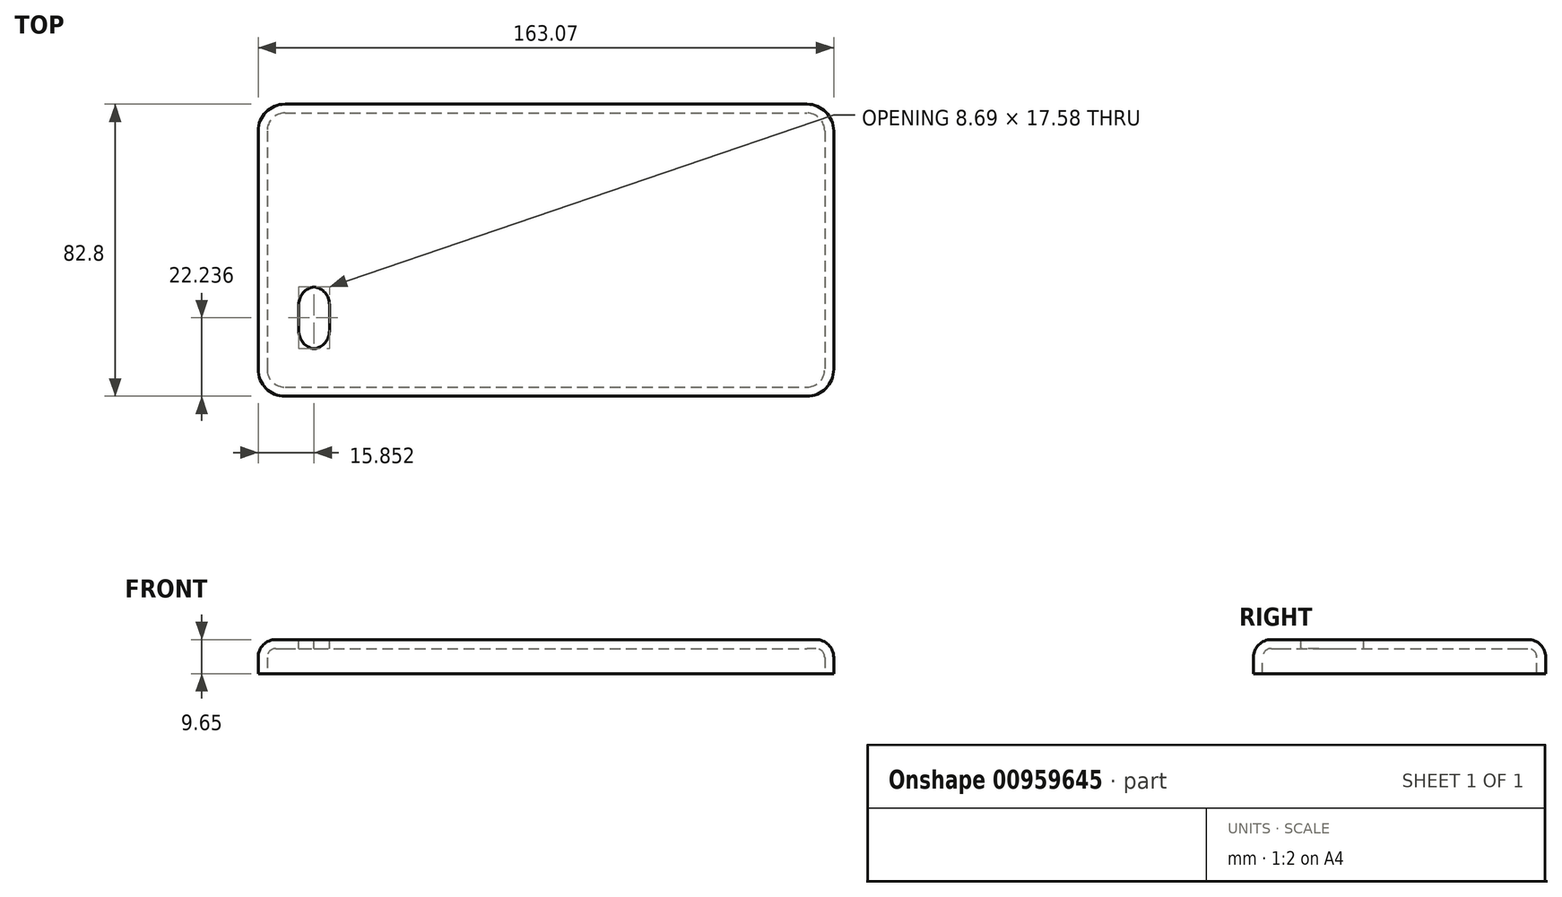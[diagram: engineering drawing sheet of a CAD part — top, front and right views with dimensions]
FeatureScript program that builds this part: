
annotation { "Feature Type Name" : "Feature", "Feature Type Description" : "" }
export const myFeature = defineFeature(function(context is Context, id is Id, definition is map)
    precondition{}
    {
        {
            var Q0;
            Q0=qCreatedBy(makeId("Top.planeOp"),FACE);
            var sketch = newSketch(context, id + "F0", { "sketchPlane" : qUnion([Q0])});
            skLineSegment(sketch, "E0.bottom", {"start": v(0, 0) * mm, "end": v(163.07, 0) * mm});
            skLineSegment(sketch, "E0.top", {"start": v(0, -82.8) * mm, "end": v(163.07, -82.8) * mm});
            skLineSegment(sketch, "E0.left", {"start": v(0, 0) * mm, "end": v(0, -82.8) * mm});
            skLineSegment(sketch, "E0.right", {"start": v(163.07, 0) * mm, "end": v(163.07, -82.8) * mm});
            skSolve(sketch);
        }
        {
            var Q0;
            Q0 = qSketchRegion(id + "F0", true);
            extrude(context, id + "F1", {"entities" : qUnion([Q0]), "depth" : 9.65 * mm, "offsetDistance" : 25.4 * mm});
        }
        {
            var Q0;
            Q0=makeQuery(id+"F1.opExtrude","SWEPT_EDGE",EDGE,{"disambiguationData":[OSD([sQuery(id+"F0.wireOp",EDGE,"E0.bottom"),sQuery(id+"F0.wireOp",EDGE,"E0.left")])]});
            var Q1;
            Q1=makeQuery(id+"F1.opExtrude","SWEPT_EDGE",EDGE,{"disambiguationData":[OSD([sQuery(id+"F0.wireOp",EDGE,"E0.bottom"),sQuery(id+"F0.wireOp",EDGE,"E0.right")])]});
            var Q2;
            Q2=makeQuery(id+"F1.opExtrude","SWEPT_EDGE",EDGE,{"disambiguationData":[OSD([sQuery(id+"F0.wireOp",EDGE,"E0.top"),sQuery(id+"F0.wireOp",EDGE,"E0.right")])]});
            var Q3;
            Q3=makeQuery(id+"F1.opExtrude","SWEPT_EDGE",EDGE,{"disambiguationData":[OSD([sQuery(id+"F0.wireOp",EDGE,"E0.top"),sQuery(id+"F0.wireOp",EDGE,"E0.left")])]});
            fillet(context, id + "F2", {"entities" : qUnion([Q0, Q1, Q2, Q3]), "radius" : 7.62 * mm, "tangentPropagation" : true, "allowEdgeOverflow" : false});
        }
        {
            var Q0;
            Q0=makeQuery(id+"F1.opExtrude","CAP_FACE",FACE,{"disambiguationData":[OSD([sQuery(id+"F0.wireOp",EDGE,"E0.bottom"),sQuery(id+"F0.wireOp",EDGE,"E0.top"),sQuery(id+"F0.wireOp",EDGE,"E0.left"),sQuery(id+"F0.wireOp",EDGE,"E0.right")])],"isStart":false});
            fillet(context, id + "F3", {"entities" : qUnion([Q0]), "radius" : 5.08 * mm, "tangentPropagation" : true, "allowEdgeOverflow" : false});
        }
        {
            var Q0;
            Q0=makeQuery(id+"F1.opExtrude","CAP_FACE",FACE,{"disambiguationData":[OSD([sQuery(id+"F0.wireOp",EDGE,"E0.bottom"),sQuery(id+"F0.wireOp",EDGE,"E0.top"),sQuery(id+"F0.wireOp",EDGE,"E0.left"),sQuery(id+"F0.wireOp",EDGE,"E0.right")])],"isStart":true});
            shell(context, id + "F4", {"entities" : qUnion([Q0]), "thickness" : 2.54 * mm});
        }
        {
            var Q0;
            Q0=makeQuery(id+"F1.opExtrude","CAP_FACE",FACE,{"disambiguationData":[OSD([sQuery(id+"F0.wireOp",EDGE,"E0.bottom"),sQuery(id+"F0.wireOp",EDGE,"E0.top"),sQuery(id+"F0.wireOp",EDGE,"E0.left"),sQuery(id+"F0.wireOp",EDGE,"E0.right")])],"isStart":false});
            var sketch = newSketch(context, id + "F5", { "sketchPlane" : qUnion([Q0])});
            skSolve(sketch);
        }
        {
            var Q0;
            {var subQ0=sQuery(id+"F0.wireOp",EDGE,"E0.right");var subQ1=sQuery(id+"F0.wireOp",EDGE,"E0.left");var subQ2=sQuery(id+"F0.wireOp",EDGE,"E0.top");var subQ3=sQuery(id+"F0.wireOp",EDGE,"E0.bottom");var subQ4=makeQuery(id+"F1.opExtrude","CAP_FACE",FACE,{"disambiguationData":[OSD([subQ3,subQ2,subQ1,subQ0])],"isStart":false});var subQ5=subQ4;Q0=makeQuery(id+"F5.imprint","IMPRINT",FACE,{"disambiguationData":[TD([[makeQuery(id+"F5.imprint","IMPRINT",EDGE,{"derivedFrom":makeQuery(id+"F3.opFillet","BLEND_EDGE",EDGE,{"blendedFrom":[makeQuery(id+"F1.opExtrude","CAP_EDGE",EDGE,{"disambiguationData":[OSD([subQ3])],"isStart":false}),subQ5],"blendedInto":[subQ5]})}),1.0]])]});}
            var sketch = newSketch(context, id + "F6", { "sketchPlane" : qUnion([Q0])});
            skLineSegment(sketch, "E1.bottom", {"start": v(11.5, -69.4) * mm, "end": v(20.2, -69.4) * mm});
            skLineSegment(sketch, "E1.top", {"start": v(11.5, -51.72) * mm, "end": v(20.2, -51.72) * mm});
            skLineSegment(sketch, "E1.left", {"start": v(11.5, -69.4) * mm, "end": v(11.5, -51.72) * mm});
            skLineSegment(sketch, "E1.right", {"start": v(20.2, -69.4) * mm, "end": v(20.2, -51.72) * mm});
            skSolve(sketch);
        }
        {
            var Q0;
            Q0=makeQuery(id+"F6.imprint","IMPRINT",FACE,{"disambiguationData":[TD([[makeQuery(id+"F6.imprint","IMPRINT",EDGE,{"derivedFrom":sQuery(id+"F6.wireOp",EDGE,"E1.bottom")}),1.0]])]});
            extrude(context, id + "F7", {"entities" : qUnion([Q0]), "operationType" : NewBodyOperationType.REMOVE, "oppositeDirection" : true, "depth" : 25.4 * mm, "offsetDistance" : 25.4 * mm});
        }
        {
            var Q0;
            Q0=makeQuery(id+"F7.boolean.opBoolean","COPY",EDGE,{"derivedFrom":makeQuery(id+"F7.opExtrude","SWEPT_EDGE",EDGE,{"disambiguationData":[OSD([sQuery(id+"F6.wireOp",EDGE,"E1.top"),sQuery(id+"F6.wireOp",EDGE,"E1.left")])]})});
            var Q1;
            Q1=makeQuery(id+"F7.boolean.opBoolean","COPY",EDGE,{"derivedFrom":makeQuery(id+"F7.opExtrude","SWEPT_EDGE",EDGE,{"disambiguationData":[OSD([sQuery(id+"F6.wireOp",EDGE,"E1.bottom"),sQuery(id+"F6.wireOp",EDGE,"E1.left")])]})});
            var Q2;
            Q2=makeQuery(id+"F7.boolean.opBoolean","COPY",EDGE,{"derivedFrom":makeQuery(id+"F7.opExtrude","SWEPT_EDGE",EDGE,{"disambiguationData":[OSD([sQuery(id+"F6.wireOp",EDGE,"E1.top"),sQuery(id+"F6.wireOp",EDGE,"E1.right")])]})});
            var Q3;
            Q3=makeQuery(id+"F7.boolean.opBoolean","COPY",EDGE,{"derivedFrom":makeQuery(id+"F7.opExtrude","SWEPT_EDGE",EDGE,{"disambiguationData":[OSD([sQuery(id+"F6.wireOp",EDGE,"E1.bottom"),sQuery(id+"F6.wireOp",EDGE,"E1.right")])]})});
            fillet(context, id + "F8", {"entities" : qUnion([Q0, Q1, Q2, Q3]), "tangentPropagation" : true, "radius" : 5.08 * mm, "defaultsChanged" : false, "vertexSettings" : [], "allowEdgeOverflow" : false});
        }
    });
